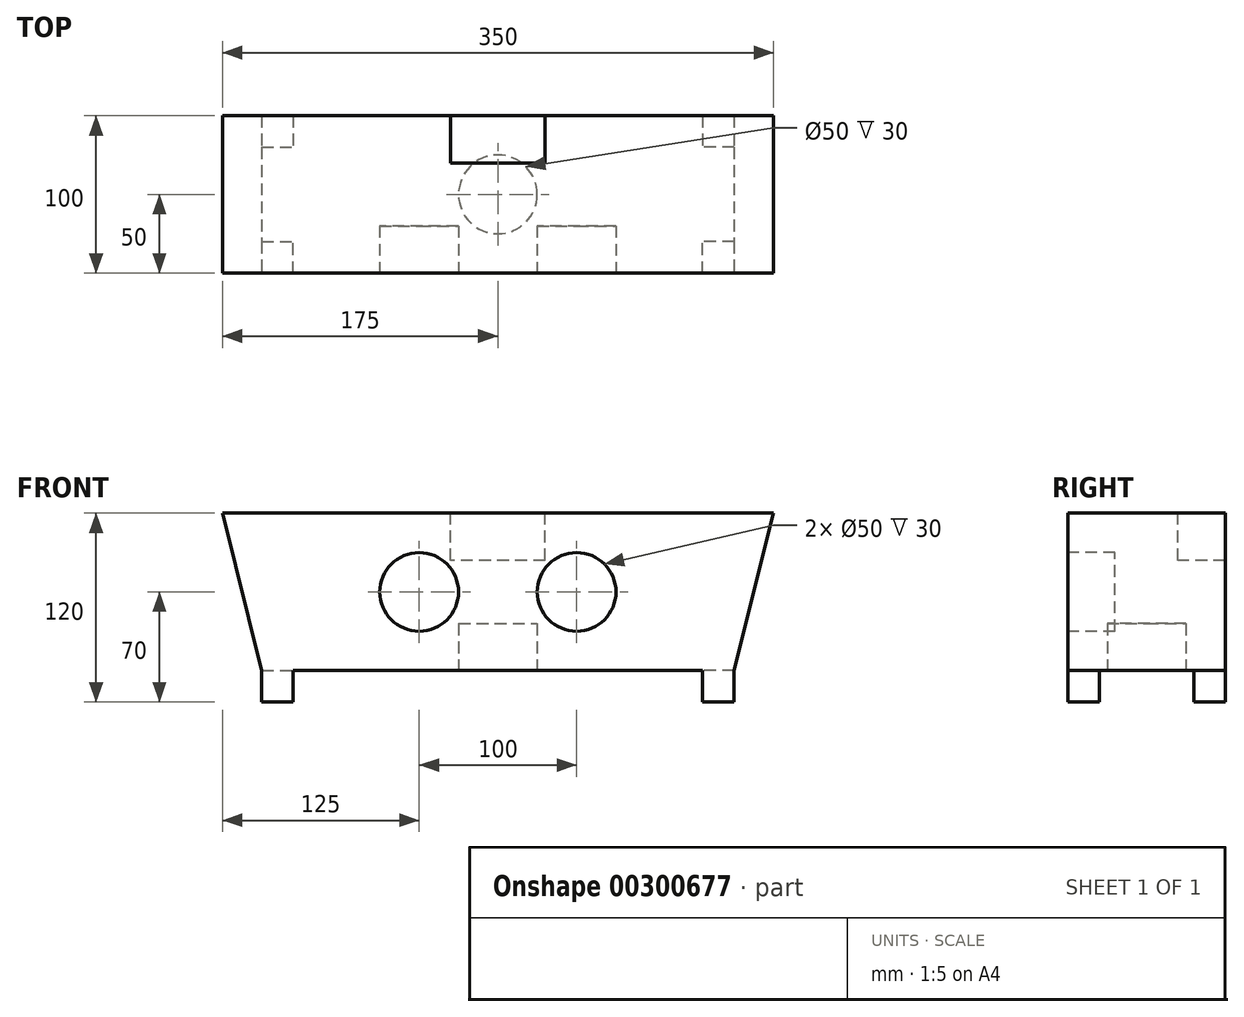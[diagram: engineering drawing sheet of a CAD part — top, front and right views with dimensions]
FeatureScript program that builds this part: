
annotation { "Feature Type Name" : "Feature", "Feature Type Description" : "" }
export const myFeature = defineFeature(function(context is Context, id is Id, definition is map)
    precondition{}
    {
        {
            var Q0;
            Q0=qCreatedBy(makeId("Front.planeOp"),FACE);
            var sketch = newSketch(context, id + "F0", { "sketchPlane" : qUnion([Q0])});
            skLineSegment(sketch, "E0.bottom", {"start": v(150, -50) * mm, "end": v(-150, -50) * mm});
            skLineSegment(sketch, "E0.top", {"start": v(150, 50) * mm, "end": v(-150, 50) * mm});
            skPoint(sketch, "E0.middle", {"position": v(0, 0) * mm});
            skLineSegment(sketch, "E1", {"start": v(-150, 50) * mm, "end": v(-175, 50) * mm});
            skLineSegment(sketch, "E2", {"start": v(-175, 50) * mm, "end": v(150, 50) * mm});
            skLineSegment(sketch, "E3", {"start": v(175, 50) * mm, "end": v(150, 50) * mm});
            skLineSegment(sketch, "E4", {"start": v(175, 50) * mm, "end": v(150, -50) * mm});
            skLineSegment(sketch, "E5", {"start": v(-175, 50) * mm, "end": v(-150, -50) * mm});
            skSolve(sketch);
        }
        {
            var Q0;
            Q0=makeQuery(id+"F0.imprint","IMPRINT",FACE,{"disambiguationData":[TD([[makeQuery(id+"F0.imprint","IMPRINT",EDGE,{"derivedFrom":sQuery(id+"F0.wireOp",EDGE,"E0.bottom")}),-1.0]])]});
            extrude(context, id + "F1", {"entities" : qUnion([Q0]), "oppositeDirection" : true, "depth" : 100 * mm});
        }
        {
            var Q0;
            Q0=makeQuery(id+"F1.opExtrude","CAP_FACE",FACE,{"disambiguationData":[OSD([sQuery(id+"F0.wireOp",EDGE,"E0.bottom"),sQuery(id+"F0.wireOp",EDGE,"E2"),sQuery(id+"F0.wireOp",EDGE,"E3"),sQuery(id+"F0.wireOp",EDGE,"E4"),sQuery(id+"F0.wireOp",EDGE,"E5")])],"isStart":true});
            var sketch = newSketch(context, id + "F2", { "sketchPlane" : qUnion([Q0])});
            skCircle(sketch, "E6", {"center": v(-50, 0) * mm, "radius": 25 * mm});
            skCircle(sketch, "E7", {"center": v(50, 0) * mm, "radius": 25 * mm});
            skSolve(sketch);
        }
        {
            var Q0;
            Q0=makeQuery(id+"F2.imprint","IMPRINT",FACE,{"disambiguationData":[TD([[makeQuery(id+"F2.imprint","IMPRINT",EDGE,{"derivedFrom":sQuery(id+"F2.wireOp",EDGE,"E7")}),1.0]])]});
            var Q1;
            Q1=makeQuery(id+"F2.imprint","IMPRINT",FACE,{"disambiguationData":[TD([[makeQuery(id+"F2.imprint","IMPRINT",EDGE,{"derivedFrom":sQuery(id+"F2.wireOp",EDGE,"E6")}),1.0]])]});
            extrude(context, id + "F3", {"entities" : qUnion([Q0, Q1]), "operationType" : NewBodyOperationType.REMOVE, "oppositeDirection" : true, "depth" : 30 * mm});
        }
        {
            var Q0;
            Q0=makeQuery(id+"F1.opExtrude","SWEPT_FACE",FACE,{"disambiguationData":[OSD([sQuery(id+"F0.wireOp",EDGE,"E0.bottom")])]});
            var sketch = newSketch(context, id + "F4", { "sketchPlane" : qUnion([Q0])});
            skPoint(sketch, "E8.endSnap0", {"position": v(0, 0) * mm});
            skCircle(sketch, "E9", {"center": v(0, -50) * mm, "radius": 25 * mm});
            skPoint(sketch, "E8.start.orphan", {"position": v(0, 0) * mm});
            skSolve(sketch);
        }
        {
            var Q0;
            Q0=makeQuery(id+"F4.imprint","IMPRINT",FACE,{"disambiguationData":[TD([[makeQuery(id+"F4.imprint","IMPRINT",EDGE,{"derivedFrom":sQuery(id+"F4.wireOp",EDGE,"E9")}),1.0]])]});
            extrude(context, id + "F5", {"entities" : qUnion([Q0]), "operationType" : NewBodyOperationType.REMOVE, "oppositeDirection" : true, "depth" : 30 * mm});
        }
        {
            var Q0;
            Q0=makeQuery(id+"F1.opExtrude","SWEPT_FACE",FACE,{"disambiguationData":[OSD([sQuery(id+"F0.wireOp",EDGE,"E2"),sQuery(id+"F0.wireOp",EDGE,"E3")])]});
            var sketch = newSketch(context, id + "F6", { "sketchPlane" : qUnion([Q0])});
            skLineSegment(sketch, "E10.bottom", {"start": v(0, 100) * mm, "end": v(-30, 100) * mm});
            skLineSegment(sketch, "E10.top", {"start": v(30, 70) * mm, "end": v(-30, 70) * mm});
            skLineSegment(sketch, "E10.left", {"start": v(30, 100) * mm, "end": v(30, 70) * mm});
            skLineSegment(sketch, "E10.right", {"start": v(-30, 100) * mm, "end": v(-30, 70) * mm});
            skSolve(sketch);
        }
        {
            var Q0;
            {var subQ1=sQuery(id+"F6.wireOp",EDGE,"E10.bottom");Q0=makeQuery(id+"F6.imprint","IMPRINT",FACE,{"disambiguationData":[TD([[makeQuery(id+"F6.imprint","IMPRINT",EDGE,{"derivedFrom":subQ1}),1.0]])]});}
            extrude(context, id + "F7", {"entities" : qUnion([Q0]), "operationType" : NewBodyOperationType.REMOVE, "oppositeDirection" : true, "depth" : 30 * mm});
        }
        {
            var Q0;
            Q0=makeQuery(id+"F1.opExtrude","SWEPT_FACE",FACE,{"disambiguationData":[OSD([sQuery(id+"F0.wireOp",EDGE,"E2"),sQuery(id+"F0.wireOp",EDGE,"E3")])]});
            var sketch = newSketch(context, id + "F8", { "sketchPlane" : qUnion([Q0])});
            skLineSegment(sketch, "E11.bottom", {"start": v(-30, 100) * mm, "end": v(30, 100) * mm});
            skLineSegment(sketch, "E11.top", {"start": v(-30, 70) * mm, "end": v(30, 70) * mm});
            skLineSegment(sketch, "E11.left", {"start": v(-30, 100) * mm, "end": v(-30, 70) * mm});
            skLineSegment(sketch, "E11.right", {"start": v(30, 100) * mm, "end": v(30, 70) * mm});
            skSolve(sketch);
        }
        {
            var Q0;
            Q0=makeQuery(id+"F1.opExtrude","SWEPT_FACE",FACE,{"disambiguationData":[OSD([sQuery(id+"F0.wireOp",EDGE,"E0.bottom")])]});
            var sketch = newSketch(context, id + "F9", { "sketchPlane" : qUnion([Q0])});
            skCircle(sketch, "E12", {"center": v(0, -50) * mm, "radius": 25 * mm});
            skCircle(sketch, "E13", {"center": v(0, -50) * mm, "radius": 12.5 * mm});
            skSolve(sketch);
        }
        {
            var Q0;
            Q0=makeQuery(id+"F9.imprint","IMPRINT",FACE,{"disambiguationData":[TD([[makeQuery(id+"F9.imprint","IMPRINT",EDGE,{"derivedFrom":sQuery(id+"F9.wireOp",EDGE,"E12")}),-1.0]])]});
            var sketch = newSketch(context, id + "F10", { "sketchPlane" : qUnion([Q0])});
            skLineSegment(sketch, "E14", {"start": v(130, 0) * mm, "end": v(150, 0) * mm});
            skLineSegment(sketch, "E15", {"start": v(150, -100) * mm, "end": v(150, -80) * mm});
            skLineSegment(sketch, "E16.top", {"start": v(150, -20) * mm, "end": v(130, -20) * mm});
            skLineSegment(sketch, "E16.left", {"start": v(150, 0) * mm, "end": v(150, -20) * mm});
            skLineSegment(sketch, "E16.right", {"start": v(130, 0) * mm, "end": v(130, -20) * mm});
            skLineSegment(sketch, "E17.bottom", {"start": v(150, -100) * mm, "end": v(130, -100) * mm});
            skLineSegment(sketch, "E17.top", {"start": v(150, -80) * mm, "end": v(130, -80) * mm});
            skLineSegment(sketch, "E17.right", {"start": v(130, -100) * mm, "end": v(130, -80) * mm});
            skLineSegment(sketch, "E18.bottom", {"start": v(-150, -100) * mm, "end": v(-130, -100) * mm});
            skLineSegment(sketch, "E18.top", {"start": v(-150, -80) * mm, "end": v(-130, -80) * mm});
            skLineSegment(sketch, "E18.left", {"start": v(-150, -100) * mm, "end": v(-150, -80) * mm});
            skLineSegment(sketch, "E18.right", {"start": v(-130, -100) * mm, "end": v(-130, -80) * mm});
            skLineSegment(sketch, "E19.bottom", {"start": v(-150, 0) * mm, "end": v(-130, 0) * mm});
            skLineSegment(sketch, "E19.top", {"start": v(-150, -20) * mm, "end": v(-130, -20) * mm});
            skLineSegment(sketch, "E19.left", {"start": v(-150, 0) * mm, "end": v(-150, -20) * mm});
            skLineSegment(sketch, "E19.right", {"start": v(-130, 0) * mm, "end": v(-130, -20) * mm});
            skSolve(sketch);
        }
        {
            var Q0;
            Q0 = qSketchRegion(id + "F10", true);
            extrude(context, id + "F11", {"entities" : qUnion([Q0]), "operationType" : NewBodyOperationType.ADD, "depth" : 20 * mm});
        }
    });
